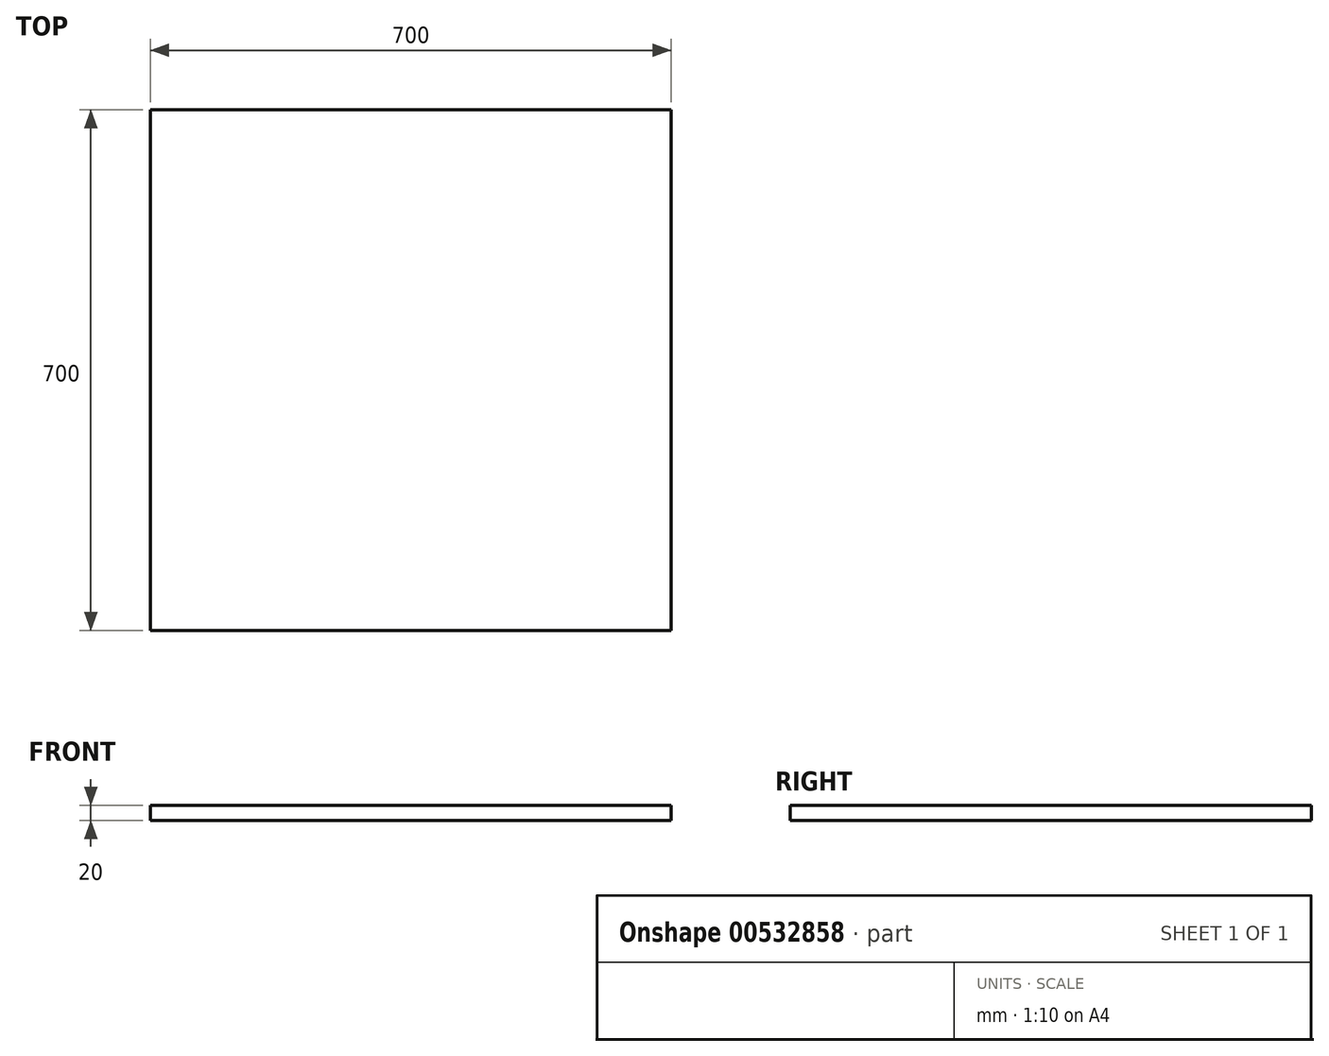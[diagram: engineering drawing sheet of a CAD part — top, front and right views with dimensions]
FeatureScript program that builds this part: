
annotation { "Feature Type Name" : "Feature", "Feature Type Description" : "" }
export const myFeature = defineFeature(function(context is Context, id is Id, definition is map)
    precondition{}
    {
        {
            var Q0;
            Q0=qCreatedBy(makeId("Top.planeOp"),FACE);
            var sketch = newSketch(context, id + "F0", { "sketchPlane" : qUnion([Q0])});
            skLineSegment(sketch, "E0.bottom", {"start": v(350, -350) * mm, "end": v(-350, -350) * mm});
            skLineSegment(sketch, "E0.top", {"start": v(350, 350) * mm, "end": v(-350, 350) * mm});
            skLineSegment(sketch, "E0.left", {"start": v(350, -350) * mm, "end": v(350, 350) * mm});
            skLineSegment(sketch, "E0.right", {"start": v(-350, -350) * mm, "end": v(-350, 350) * mm});
            skPoint(sketch, "E0.middle", {"position": v(0, 0) * mm});
            skSolve(sketch);
        }
        {
            var Q0;
            Q0=makeQuery(id+"F0.imprint","IMPRINT",FACE,{"disambiguationData":[TD([[makeQuery(id+"F0.imprint","IMPRINT",EDGE,{"derivedFrom":sQuery(id+"F0.wireOp",EDGE,"E0.bottom")}),-1.0]])]});
            extrude(context, id + "F1", {"entities" : qUnion([Q0]), "depth" : 20 * mm});
        }
    });
